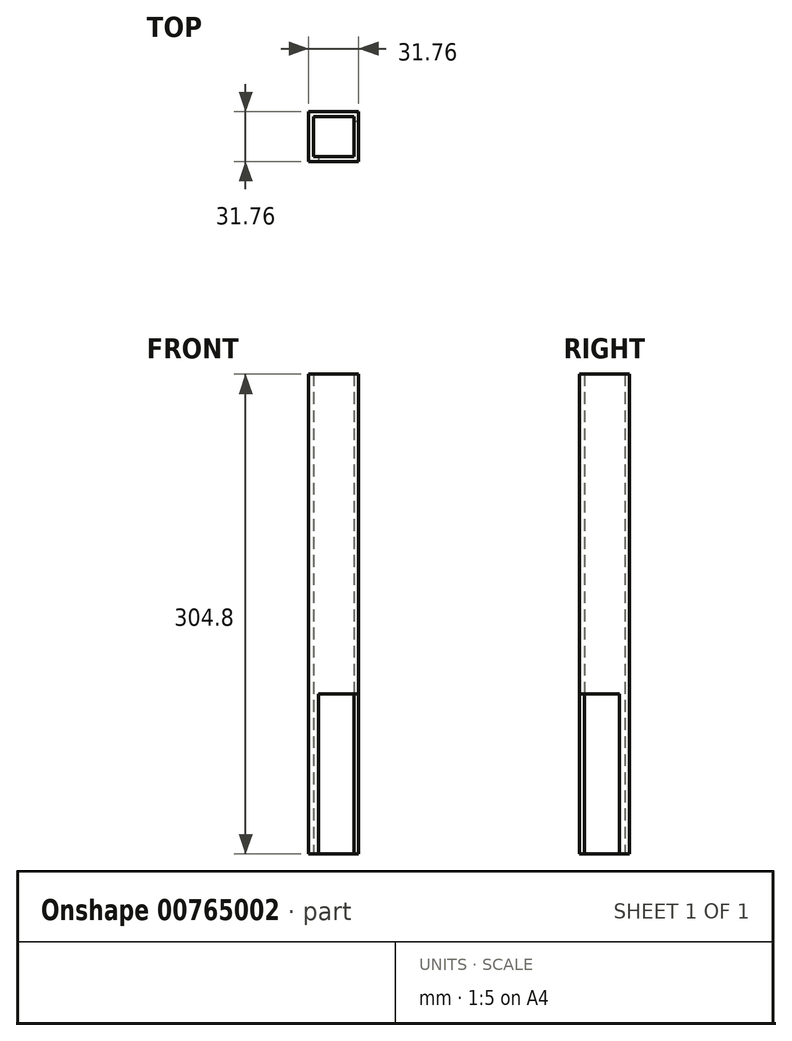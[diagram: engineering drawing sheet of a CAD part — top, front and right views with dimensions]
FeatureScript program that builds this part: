
annotation { "Feature Type Name" : "Feature", "Feature Type Description" : "" }
export const myFeature = defineFeature(function(context is Context, id is Id, definition is map)
    precondition{}
    {
        {
            var Q0;
            Q0=qCreatedBy(makeId("Top.planeOp"),FACE);
            var sketch = newSketch(context, id + "F0", { "sketchPlane" : qUnion([Q0])});
            skLineSegment(sketch, "E0.bottom", {"start": v(15.88, 15.88) * mm, "end": v(-15.88, 15.88) * mm});
            skLineSegment(sketch, "E0.top", {"start": v(15.88, -15.88) * mm, "end": v(-15.88, -15.88) * mm});
            skLineSegment(sketch, "E0.left", {"start": v(15.88, 15.88) * mm, "end": v(15.88, -15.88) * mm});
            skLineSegment(sketch, "E0.right", {"start": v(-15.88, 15.88) * mm, "end": v(-15.88, -15.88) * mm});
            skPoint(sketch, "E0.middle", {"position": v(0, 0) * mm});
            skLineSegment(sketch, "E1.0", {"start": v(-12.83, 12.83) * mm, "end": v(-12.83, -12.83) * mm});
            skLineSegment(sketch, "E1.1", {"start": v(12.83, 12.83) * mm, "end": v(-12.83, 12.83) * mm});
            skLineSegment(sketch, "E1.2", {"start": v(12.83, 12.83) * mm, "end": v(12.83, -12.83) * mm});
            skLineSegment(sketch, "E1.3", {"start": v(12.83, -12.83) * mm, "end": v(-12.83, -12.83) * mm});
            skSolve(sketch);
        }
        {
            var Q0;
            Q0 = qSketchRegion(id + "F0", true);
            extrude(context, id + "F1", {"entities" : qUnion([Q0]), "depth" : 304.8 * mm, "offsetDistance" : 25.4 * mm});
        }
        {
            var Q0;
            Q0=makeQuery(id+"F1.opExtrude","SWEPT_FACE",FACE,{"disambiguationData":[OSD([sQuery(id+"F0.wireOp",EDGE,"E0.top")])]});
            var sketch = newSketch(context, id + "F2", { "sketchPlane" : qUnion([Q0])});
            skLineSegment(sketch, "E2.0", {"start": v(15.88, 0) * mm, "end": v(-9.52, 0) * mm});
            skLineSegment(sketch, "E2.1", {"start": v(15.88, 101.6) * mm, "end": v(15.88, 0) * mm});
            skLineSegment(sketch, "E3", {"start": v(-9.52, 0) * mm, "end": v(-9.53, 101.6) * mm});
            skLineSegment(sketch, "E4", {"start": v(-9.53, 101.6) * mm, "end": v(15.88, 101.6) * mm});
            skPoint(sketch, "E5.orphan", {"position": v(-15.88, 0) * mm});
            skPoint(sketch, "E6.orphan", {"position": v(15.88, 304.8) * mm});
            skSolve(sketch);
        }
        {
            var Q0;
            Q0 = qSketchRegion(id + "F2", true);
            extrude(context, id + "F3", {"entities" : qUnion([Q0]), "operationType" : NewBodyOperationType.REMOVE, "oppositeDirection" : true, "depth" : 25.4 * mm, "offsetDistance" : 25.4 * mm});
        }
    });
